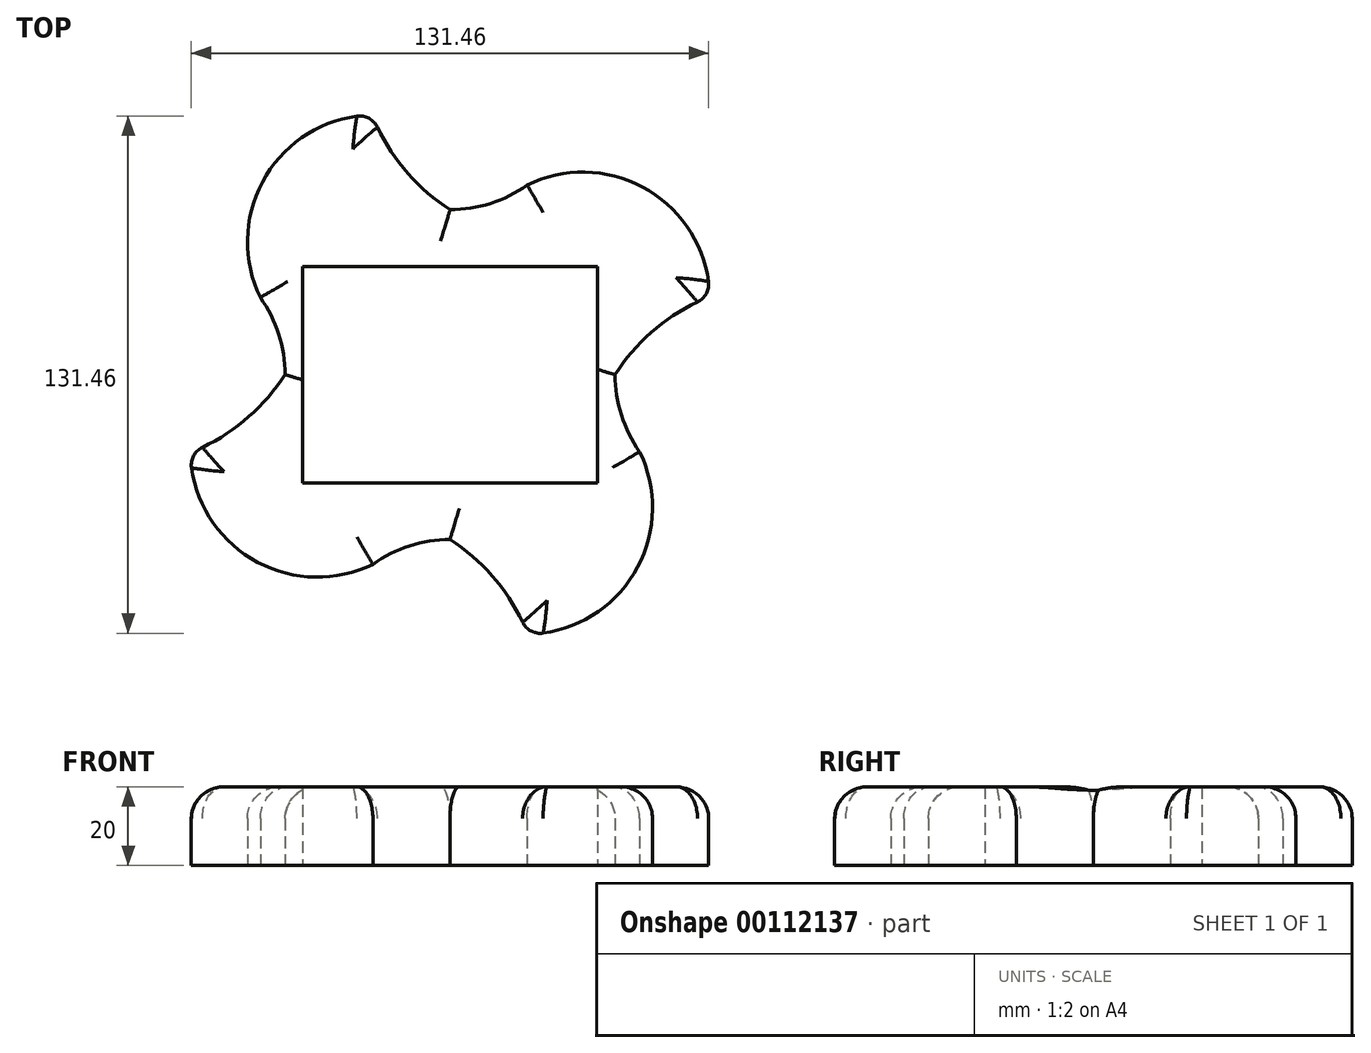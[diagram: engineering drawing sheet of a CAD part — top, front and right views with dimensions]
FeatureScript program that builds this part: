
annotation { "Feature Type Name" : "Feature", "Feature Type Description" : "" }
export const myFeature = defineFeature(function(context is Context, id is Id, definition is map)
    precondition{}
    {
        {
            var Q0;
            Q0=qCreatedBy(makeId("Top.planeOp"),FACE);
            var sketch = newSketch(context, id + "F0", { "sketchPlane" : qUnion([Q0])});
            skPoint(sketch, "E0.middle", {"position": v(0, 0) * mm});
            skArc(sketch, "E1", {"start": v(-19.8, 65.98) * mm, "mid": v(-46.71, 50.56) * mm, "end": v(-48.18, 19.59) * mm});
            skPoint(sketch, "E2", {"position": v(-75.62, 0) * mm});
            skArc(sketch, "E3", {"start": v(-48.18, 19.59) * mm, "mid": v(-43.51, 10.29) * mm, "end": v(-41.9, 0) * mm});
            skArc(sketch, "E4", {"start": v(-19.8, 65.98) * mm, "mid": v(-11.78, 52.4) * mm, "end": v(0, 41.9) * mm});
            skArc(sketch, "E5.1.0", {"start": v(-65.98, -19.8) * mm, "mid": v(-50.56, -46.71) * mm, "end": v(-19.59, -48.18) * mm});
            skArc(sketch, "E5.1.1", {"start": v(-65.98, -19.8) * mm, "mid": v(-52.4, -11.78) * mm, "end": v(-41.9, 0) * mm});
            skArc(sketch, "E5.1.2", {"start": v(-19.59, -48.18) * mm, "mid": v(-10.29, -43.51) * mm, "end": v(0, -41.9) * mm});
            skArc(sketch, "E5.2.0", {"start": v(19.8, -65.98) * mm, "mid": v(46.71, -50.56) * mm, "end": v(48.18, -19.59) * mm});
            skArc(sketch, "E5.2.1", {"start": v(19.8, -65.98) * mm, "mid": v(11.78, -52.4) * mm, "end": v(0, -41.9) * mm});
            skArc(sketch, "E5.2.2", {"start": v(48.18, -19.59) * mm, "mid": v(43.51, -10.29) * mm, "end": v(41.9, 0) * mm});
            skArc(sketch, "E5.3.0", {"start": v(65.98, 19.8) * mm, "mid": v(50.56, 46.71) * mm, "end": v(19.59, 48.18) * mm});
            skArc(sketch, "E5.3.1", {"start": v(65.98, 19.8) * mm, "mid": v(52.4, 11.78) * mm, "end": v(41.9, 0) * mm});
            skArc(sketch, "E5.3.2", {"start": v(19.59, 48.18) * mm, "mid": v(10.29, 43.51) * mm, "end": v(0, 41.9) * mm});
            skLineSegment(sketch, "E6.bottom", {"start": v(-37.5, 27.5) * mm, "end": v(37.5, 27.5) * mm});
            skLineSegment(sketch, "E6.top", {"start": v(-37.5, -27.5) * mm, "end": v(37.5, -27.5) * mm});
            skLineSegment(sketch, "E6.left", {"start": v(-37.5, 27.5) * mm, "end": v(-37.5, -27.5) * mm});
            skLineSegment(sketch, "E6.right", {"start": v(37.5, 27.5) * mm, "end": v(37.5, -27.5) * mm});
            skSolve(sketch);
        }
        {
            var Q0;
            Q0=makeQuery(id+"F0.imprint","IMPRINT",FACE,{"disambiguationData":[TD([[makeQuery(id+"F0.imprint","IMPRINT",EDGE,{"derivedFrom":sQuery(id+"F0.wireOp",EDGE,"E1")}),1.0]])]});
            extrude(context, id + "F1", {"entities" : qUnion([Q0]), "depth" : 20 * mm});
        }
        {
            var Q0;
            Q0=makeQuery(id+"F1.opExtrude","CAP_EDGE",EDGE,{"disambiguationData":[OSD([sQuery(id+"F0.wireOp",EDGE,"E5.1.1")])],"isStart":false});
            var Q1;
            Q1=makeQuery(id+"F1.opExtrude","CAP_EDGE",EDGE,{"disambiguationData":[OSD([sQuery(id+"F0.wireOp",EDGE,"E1")])],"isStart":false});
            var Q2;
            Q2=makeQuery(id+"F1.opExtrude","CAP_EDGE",EDGE,{"disambiguationData":[OSD([sQuery(id+"F0.wireOp",EDGE,"E3")])],"isStart":false});
            var Q3;
            Q3=makeQuery(id+"F1.opExtrude","CAP_EDGE",EDGE,{"disambiguationData":[OSD([sQuery(id+"F0.wireOp",EDGE,"E5.2.1")])],"isStart":false});
            var Q4;
            Q4=makeQuery(id+"F1.opExtrude","CAP_EDGE",EDGE,{"disambiguationData":[OSD([sQuery(id+"F0.wireOp",EDGE,"E5.1.2")])],"isStart":false});
            var Q5;
            Q5=makeQuery(id+"F1.opExtrude","CAP_EDGE",EDGE,{"disambiguationData":[OSD([sQuery(id+"F0.wireOp",EDGE,"E5.1.0")])],"isStart":false});
            var Q6;
            Q6=makeQuery(id+"F1.opExtrude","CAP_EDGE",EDGE,{"disambiguationData":[OSD([sQuery(id+"F0.wireOp",EDGE,"E5.2.0")])],"isStart":false});
            var Q7;
            Q7=makeQuery(id+"F1.opExtrude","CAP_EDGE",EDGE,{"disambiguationData":[OSD([sQuery(id+"F0.wireOp",EDGE,"E5.2.2")])],"isStart":false});
            var Q8;
            Q8=makeQuery(id+"F1.opExtrude","CAP_EDGE",EDGE,{"disambiguationData":[OSD([sQuery(id+"F0.wireOp",EDGE,"E5.3.1")])],"isStart":false});
            var Q9;
            Q9=makeQuery(id+"F1.opExtrude","CAP_EDGE",EDGE,{"disambiguationData":[OSD([sQuery(id+"F0.wireOp",EDGE,"E5.3.0")])],"isStart":false});
            var Q10;
            Q10=makeQuery(id+"F1.opExtrude","CAP_EDGE",EDGE,{"disambiguationData":[OSD([sQuery(id+"F0.wireOp",EDGE,"E5.3.2")])],"isStart":false});
            var Q11;
            Q11=makeQuery(id+"F1.opExtrude","CAP_EDGE",EDGE,{"disambiguationData":[OSD([sQuery(id+"F0.wireOp",EDGE,"E4")])],"isStart":false});
            fillet(context, id + "F2", {"entities" : qUnion([Q0, Q1, Q2, Q3, Q4, Q5, Q6, Q7, Q8, Q9, Q10, Q11]), "radius" : 8 * mm, "allowEdgeOverflow" : false});
        }
        {
            var Q0;
            Q0=makeQuery(id+"F1.opExtrude","SWEPT_EDGE",EDGE,{"disambiguationData":[OSD([sQuery(id+"F0.wireOp",EDGE,"E5.2.0"),sQuery(id+"F0.wireOp",EDGE,"E5.2.1")])]});
            var Q1;
            Q1=makeQuery(id+"F1.opExtrude","SWEPT_EDGE",EDGE,{"disambiguationData":[OSD([sQuery(id+"F0.wireOp",EDGE,"E5.1.0"),sQuery(id+"F0.wireOp",EDGE,"E5.1.1")])]});
            var Q2;
            Q2=makeQuery(id+"F1.opExtrude","SWEPT_EDGE",EDGE,{"disambiguationData":[OSD([sQuery(id+"F0.wireOp",EDGE,"E1"),sQuery(id+"F0.wireOp",EDGE,"E4")])]});
            var Q3;
            Q3=makeQuery(id+"F1.opExtrude","SWEPT_EDGE",EDGE,{"disambiguationData":[OSD([sQuery(id+"F0.wireOp",EDGE,"E5.3.0"),sQuery(id+"F0.wireOp",EDGE,"E5.3.1")])]});
            fillet(context, id + "F3", {"entities" : qUnion([Q0, Q1, Q2, Q3]), "radius" : 5 * mm, "tangentPropagation" : true, "allowEdgeOverflow" : false});
        }
    });
